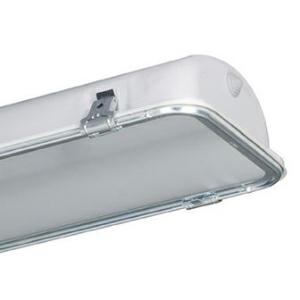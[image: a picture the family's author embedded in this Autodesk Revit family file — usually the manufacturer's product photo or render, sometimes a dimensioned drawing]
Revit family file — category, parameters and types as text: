
# Revit family: 3f_filippi_-_beta_i3f_76_vs_ampio_3f_filippi_-_55145_-_i3f_led_762x12w_ep_ampio_vs_l655
name_source: partatom
category: Lighting Fixtures
units: mm (PartAtom-declared; Revit-internal decimal feet)

## family parameters
Cut with Voids When Loaded = No
Host = Face
Light Source = No
Part Type = Normal
Room Calculation Point = No
Round Connector Dimension = Use Diameter
Shared = No

## types (1)
- 3F Filippi - Beta i3F 76 VS Ampio (1 x LED, 3591 lm, 29 W, 4000 K)
    Apparent Load = 29 VA
    Approval mark = ENEC
    CIE Flux Codes = 62 90 98 100 100
    Color Rendering = 80
    Color Temperature = 4000 K
    Control Gear = Electronic ballast
    Default Elevation = 1800 mm
    Description = ILLUMINOTECHNICAL
Luminous efficiency 100% (DLOR 100%, ULOR 0%).
Initial luminous flux of the luminaire 3591 lm.
Emergency luminaire luminous flux BLF 14.3%.
Wide symmetric distribution.
Installation Interdistance Transv.D = 1.31 x hu - Long.D = 1.31 x hu.
Tabular UGR (CIE 117 - 4H-8H; S=0.25H; 70/50/20): RUG 19.9 - 21.1.
Beam angle: 90° - 99°.
Luminous efficacy 124 lm/W.
Lifetime (L93/B10): 30000 h. (tq+25°C)
Lifetime (L90/B10): 50000 h. (tq+25°C)
Lifetime (L85/B10): 80000 h. (tq+25°C)
Lifetime (L80/B10): 100000 h. (tq+25°C)
Sudden decreased luminous flux after 50000 hours: 0% (C0).
Photobiological safety in compliance with IEC/TR 62778: RG0 risk exempt, (IEC 62471).
In compliance with IEC/EN 62722-2-1 - IEC/EN 62717 standards.

SOURCE
2 linear LED modules 12W/840.
Energy efficiency class (UE 2019/2020 - UE 2019/2015): D.
CIE 13.3 Colour rendering index: CRI >80 (R9 <50%).
IES TM-30 Fidelity Index: Rf = 84 Rg = 95.
CCT nominal colour temperature 4000 K.
Colour initial tolerance (MacAdam): SDCM 3.

MECHANICAL
Single-piece housing in pressed steel, powder-coated in white epoxy-polyester.
Moulded anti-glare glass, non-combustible, tempered, mounted and locked to the single-piece galvanised steel perimetrical frame, sealing gasket, hinged opening by means of galvanised steel clips.
Wide flow recuperator, oversized, in specular aluminium with superficial titanium-magnesium treatment, non-iridescent.
Gear-tray unit in hot-galvanised steel, painted in white polyester, fixed to the housing by means of "Ribloc" rapid devices in galvanised steel, hinged opening.
Luminaire with limited surface temperature. - D - (EN 60598-2-24)
Dimensions: 655x235 mm, height 110 mm. Weight 4.75 kg.
IP65 protection degree.
Mechanical strength to impacts IK09 (10 joule).
Glow-wire test resistance 960°C.

ELECTRICAL
Halogen Free electronic wiring 230V-50/60Hz, power factor 0.85, THD <25%, constant output current, SELV, class I, 1 driver.
Power of the luminaire 29 W.
CE - IEC 60598-1 - EN 60598-1.
EP maintained emergency wiring on board, 1h duration, 24h recharge; compliant with EN 60598-2-22, excluding high risk areas.
SAFE FLICKER: PstLM=<1 and SVM=<0.4 (IEC TR 61547-1 and IEC TR 63158), to ensure a more comfortable and safe light.
Ambient temperature from +5°C to +25°C.
Temperature class T6 max 85°C.
Relative humidity UR: <85%.

INSTALLATION
Ceiling / Suspended / Wall.
All accessories dedicated to this product are available on the Catalog and on our website www.3F-Filippi.com.

APPLICATIONS
In industrial environments, stores and dry, dusty indoor environments, subject to occasional water splashes.

WARNING
Fixture not suitable for cold stores with an ambient temperature <5°C and/or relative humidity >85%.
Luminaire designed for disposal/recycling at end-of-life.
Replaceable (LED only) light source by a professional. Replaceable control gear by a professional.
    Height = 110 mm
    Lamp = 1 x LED
    Lamp Light Flux = 3591 lm
    Lamp Power = 29 W
    Lamp count = 1
    Length = 655 mm
    Lifetime = 50000 h
    Luminous efficacy = 124 lm/W
    Manufacturer = 3F Filippi
    ModVariant = No
    Model = 3F Filippi - 55145 - i3F LED 762x12W EP AMPIO VS L655
    Mounting Place = Ceiling
    Mounting Type = Pendant
    Number of Poles = 1
    OnlyDefault = Yes
    Power Factor = 1
    Product Name = 3F Filippi - Beta i3F 76 VS Ampio
    Product group = pendant luminaire
    ProductGroupID = 9
    Protection Class = Protection class I
    Protection Degree = IP 65
    RLX_Detail_Level = 1
    RLX_Emergency_Light_Flux = 0 lm
    RLX_Emergency_Type = 0
    RLX_Emergency_Type_DB = No
    RlxData = <blob elided: 61945 chars, md5=80a84e7e>
    Socket = socket
    Standby Power = 0 W
    System Light Flux = 3591 lm
    System Power = 29 W
    Type Comments = Product without accessories
    Type Image = 3ffilippi_55145.jpg
    URL = http://relux.com
    VarID = ---
    Voltage = 0 V
    Weight = 0.00 kg
    Width = 235 mm

## geometry (parser evidence)
native form markers: Blend x4, Sweep x11
no freeform markers — native parametric forms only
